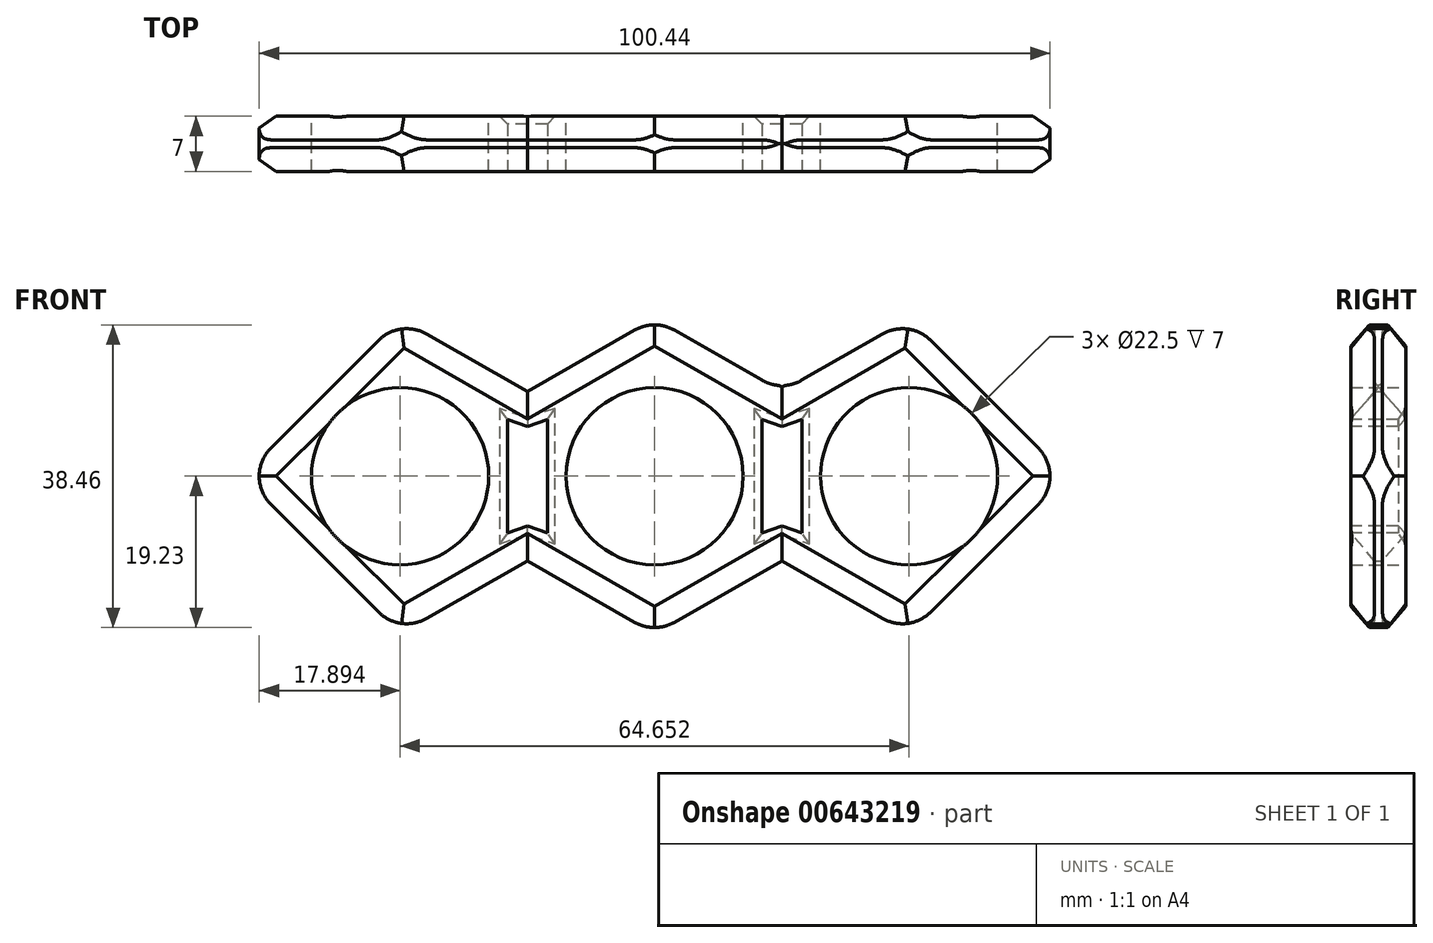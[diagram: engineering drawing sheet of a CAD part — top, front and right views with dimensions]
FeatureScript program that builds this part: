
annotation { "Feature Type Name" : "Feature", "Feature Type Description" : "" }
export const myFeature = defineFeature(function(context is Context, id is Id, definition is map)
    precondition{}
    {
        {
            var Q0;
            Q0=qCreatedBy(makeId("Front.planeOp"),FACE);
            var sketch = newSketch(context, id + "F0", { "sketchPlane" : qUnion([Q0])});
            skCircle(sketch, "E0", {"center": v(0, 0) * mm, "radius": 11.25 * mm});
            skCircle(sketch, "E1", {"center": v(-32.33, 0) * mm, "radius": 11.25 * mm});
            skCircle(sketch, "E2", {"center": v(32.33, 0) * mm, "radius": 11.25 * mm});
            skLineSegment(sketch, "E3", {"start": v(-32.33, 0) * mm, "end": v(-52.33, 0) * mm});
            skLineSegment(sketch, "E4.MirrorCS", {"start": v(32.33, 0) * mm, "end": v(52.33, 0) * mm});
            skLineSegment(sketch, "E5", {"start": v(-32.33, 0) * mm, "end": v(-32.33, 20) * mm});
            skLineSegment(sketch, "E6", {"start": v(-32.33, 0) * mm, "end": v(-32.33, -20) * mm});
            skLineSegment(sketch, "E7", {"start": v(-52.33, 0) * mm, "end": v(-32.33, -20) * mm});
            skLineSegment(sketch, "E8", {"start": v(-52.33, 0) * mm, "end": v(-32.33, 20) * mm});
            skLineSegment(sketch, "E9", {"start": v(-16.16, 0) * mm, "end": v(-16.16, 10.75) * mm});
            skLineSegment(sketch, "E10", {"start": v(-16.16, 10.75) * mm, "end": v(-32.33, 20) * mm});
            skLineSegment(sketch, "E11.MirrorCS", {"start": v(-16.16, -10.75) * mm, "end": v(-32.33, -20) * mm});
            skLineSegment(sketch, "E12.MirrorCS", {"start": v(-16.16, 0) * mm, "end": v(-16.16, -10.75) * mm});
            skLineSegment(sketch, "E13", {"start": v(0, 0) * mm, "end": v(0, 20) * mm});
            skLineSegment(sketch, "E14", {"start": v(0, 0) * mm, "end": v(0, -20) * mm});
            skLineSegment(sketch, "E15", {"start": v(-16.16, 10.75) * mm, "end": v(0, 20) * mm});
            skLineSegment(sketch, "E16", {"start": v(-16.16, -10.75) * mm, "end": v(0, -20) * mm});
            skLineSegment(sketch, "E17.MirrorCS", {"start": v(16.16, 10.75) * mm, "end": v(0, 20) * mm});
            skLineSegment(sketch, "E18.MirrorCS", {"start": v(16.16, -10.75) * mm, "end": v(0, -20) * mm});
            skLineSegment(sketch, "E19.MirrorCS", {"start": v(52.33, 0) * mm, "end": v(32.33, -20) * mm});
            skLineSegment(sketch, "E20.MirrorCS", {"start": v(52.33, 0) * mm, "end": v(32.33, 20) * mm});
            skLineSegment(sketch, "E21.MirrorCS", {"start": v(16.16, 10.75) * mm, "end": v(32.33, 20) * mm});
            skLineSegment(sketch, "E22.MirrorCS", {"start": v(16.16, -10.75) * mm, "end": v(32.33, -20) * mm});
            skLineSegment(sketch, "E23.MirrorCS", {"start": v(16.16, 0) * mm, "end": v(16.16, 10.75) * mm});
            skLineSegment(sketch, "E24.MirrorCS", {"start": v(16.16, 0) * mm, "end": v(16.16, -10.75) * mm});
            skLineSegment(sketch, "E25", {"start": v(-21.08, 0) * mm, "end": v(-11.25, 0) * mm});
            skLineSegment(sketch, "E26", {"start": v(11.25, 0) * mm, "end": v(21.08, 0) * mm});
            skSolve(sketch);
        }
        {
            var Q0;
            {var subQ0=sQuery(id+"F0.wireOp",EDGE,"E20.MirrorCS");Q0=makeQuery(id+"F0.imprint","IMPRINT",FACE,{"disambiguationData":[TD([[makeQuery(id+"F0.imprint","IMPRINT",EDGE,{"derivedFrom":subQ0}),1.0]])]});}
            var Q1;
            {var subQ0=sQuery(id+"F0.wireOp",EDGE,"E19.MirrorCS");Q1=makeQuery(id+"F0.imprint","IMPRINT",FACE,{"disambiguationData":[TD([[makeQuery(id+"F0.imprint","IMPRINT",EDGE,{"derivedFrom":subQ0}),-1.0]])]});}
            var Q2;
            {var subQ0=sQuery(id+"F0.wireOp",EDGE,"E18.MirrorCS");Q2=makeQuery(id+"F0.imprint","IMPRINT",FACE,{"disambiguationData":[TD([[makeQuery(id+"F0.imprint","IMPRINT",EDGE,{"derivedFrom":subQ0}),-1.0]])]});}
            var Q3;
            {var subQ0=sQuery(id+"F0.wireOp",EDGE,"E17.MirrorCS");Q3=makeQuery(id+"F0.imprint","IMPRINT",FACE,{"disambiguationData":[TD([[makeQuery(id+"F0.imprint","IMPRINT",EDGE,{"derivedFrom":subQ0}),1.0]])]});}
            var Q4;
            {var subQ4=sQuery(id+"F0.wireOp",EDGE,"E9");Q4=makeQuery(id+"F0.imprint","IMPRINT",FACE,{"disambiguationData":[TD([[makeQuery(id+"F0.imprint","IMPRINT",EDGE,{"derivedFrom":subQ4}),-1.0]])]});}
            var Q5;
            {var subQ0=sQuery(id+"F0.wireOp",EDGE,"E12.MirrorCS");Q5=makeQuery(id+"F0.imprint","IMPRINT",FACE,{"disambiguationData":[TD([[makeQuery(id+"F0.imprint","IMPRINT",EDGE,{"derivedFrom":subQ0}),1.0]])]});}
            var Q6;
            {var subQ0=sQuery(id+"F0.wireOp",EDGE,"E11.MirrorCS");Q6=makeQuery(id+"F0.imprint","IMPRINT",FACE,{"disambiguationData":[TD([[makeQuery(id+"F0.imprint","IMPRINT",EDGE,{"derivedFrom":subQ0}),-1.0]])]});}
            var Q7;
            {var subQ5=sQuery(id+"F0.wireOp",EDGE,"E7");Q7=makeQuery(id+"F0.imprint","IMPRINT",FACE,{"disambiguationData":[TD([[makeQuery(id+"F0.imprint","IMPRINT",EDGE,{"derivedFrom":subQ5}),1.0]])]});}
            var Q8;
            {var subQ5=sQuery(id+"F0.wireOp",EDGE,"E8");Q8=makeQuery(id+"F0.imprint","IMPRINT",FACE,{"disambiguationData":[TD([[makeQuery(id+"F0.imprint","IMPRINT",EDGE,{"derivedFrom":subQ5}),-1.0]])]});}
            var Q9;
            {var subQ0=sQuery(id+"F0.wireOp",EDGE,"E9");Q9=makeQuery(id+"F0.imprint","IMPRINT",FACE,{"disambiguationData":[TD([[makeQuery(id+"F0.imprint","IMPRINT",EDGE,{"derivedFrom":subQ0}),1.0]])]});}
            extrude(context, id + "F1", {"entities" : qUnion([Q0, Q1, Q2, Q3, Q4, Q5, Q6, Q7, Q8, Q9]), "depth" : 7 * mm, "offsetDistance" : 25.4 * mm});
        }
        {
            var Q0;
            Q0=makeQuery(id+"F1.opExtrude","CAP_FACE",FACE,{"disambiguationData":[OSD([sQuery(id+"F0.wireOp",EDGE,"E0"),sQuery(id+"F0.wireOp",EDGE,"E1"),sQuery(id+"F0.wireOp",EDGE,"E2"),sQuery(id+"F0.wireOp",EDGE,"E7"),sQuery(id+"F0.wireOp",EDGE,"E8"),sQuery(id+"F0.wireOp",EDGE,"E10"),sQuery(id+"F0.wireOp",EDGE,"E11.MirrorCS"),sQuery(id+"F0.wireOp",EDGE,"E15"),sQuery(id+"F0.wireOp",EDGE,"E16"),sQuery(id+"F0.wireOp",EDGE,"E17.MirrorCS"),sQuery(id+"F0.wireOp",EDGE,"E18.MirrorCS"),sQuery(id+"F0.wireOp",EDGE,"E19.MirrorCS"),sQuery(id+"F0.wireOp",EDGE,"E20.MirrorCS"),sQuery(id+"F0.wireOp",EDGE,"E21.MirrorCS"),sQuery(id+"F0.wireOp",EDGE,"E22.MirrorCS")])],"isStart":false});
            var sketch = newSketch(context, id + "F2", { "sketchPlane" : qUnion([Q0])});
            skLineSegment(sketch, "E27", {"start": v(16.16, -8.44) * mm, "end": v(16.16, 8.44) * mm});
            skLineSegment(sketch, "E28", {"start": v(-16.16, -8.44) * mm, "end": v(-16.16, 8.44) * mm});
            skLineSegment(sketch, "E29", {"start": v(13.63, -9.9) * mm, "end": v(13.63, 9.9) * mm});
            skLineSegment(sketch, "E30", {"start": v(13.63, 9.9) * mm, "end": v(18.7, 9.9) * mm});
            skLineSegment(sketch, "E31", {"start": v(18.7, 9.9) * mm, "end": v(18.7, -9.9) * mm});
            skLineSegment(sketch, "E32", {"start": v(13.63, -9.9) * mm, "end": v(16.16, -8.44) * mm});
            skLineSegment(sketch, "E33", {"start": v(16.16, -8.44) * mm, "end": v(18.7, -9.9) * mm});
            skLineSegment(sketch, "E34", {"start": v(13.63, 9.9) * mm, "end": v(16.16, 8.44) * mm});
            skLineSegment(sketch, "E35", {"start": v(16.16, 8.44) * mm, "end": v(18.7, 9.9) * mm});
            skLineSegment(sketch, "E36.MirrorCS", {"start": v(-13.63, -9.9) * mm, "end": v(-13.63, 9.9) * mm});
            skLineSegment(sketch, "E37.MirrorCS", {"start": v(-18.7, 9.9) * mm, "end": v(-18.7, -9.9) * mm});
            skLineSegment(sketch, "E38.MirrorCS", {"start": v(-16.16, 8.44) * mm, "end": v(-18.7, 9.9) * mm});
            skLineSegment(sketch, "E39.MirrorCS", {"start": v(-13.63, 9.9) * mm, "end": v(-16.16, 8.44) * mm});
            skLineSegment(sketch, "E40.MirrorCS", {"start": v(-16.16, -8.44) * mm, "end": v(-18.7, -9.9) * mm});
            skLineSegment(sketch, "E41.MirrorCS", {"start": v(-13.63, -9.9) * mm, "end": v(-16.16, -8.44) * mm});
            skLineSegment(sketch, "E42", {"start": v(-18.7, 7.21) * mm, "end": v(-16.16, 6.34) * mm});
            skLineSegment(sketch, "E43", {"start": v(-16.16, 6.34) * mm, "end": v(-13.63, 7.21) * mm});
            skLineSegment(sketch, "E44.MirrorCS", {"start": v(-16.16, -6.34) * mm, "end": v(-13.63, -7.21) * mm});
            skLineSegment(sketch, "E45.MirrorCS", {"start": v(-18.7, -7.21) * mm, "end": v(-16.16, -6.34) * mm});
            skLineSegment(sketch, "E46.MirrorCS", {"start": v(16.16, 6.34) * mm, "end": v(13.63, 7.21) * mm});
            skLineSegment(sketch, "E47.MirrorCS", {"start": v(18.7, 7.21) * mm, "end": v(16.16, 6.34) * mm});
            skLineSegment(sketch, "E48.MirrorCS", {"start": v(16.16, -6.34) * mm, "end": v(13.63, -7.21) * mm});
            skLineSegment(sketch, "E49.MirrorCS", {"start": v(18.7, -7.21) * mm, "end": v(16.16, -6.34) * mm});
            skSolve(sketch);
        }
        {
            var Q0;
            {var subQ0=sQuery(id+"F2.wireOp",EDGE,"E43");Q0=makeQuery(id+"F2.imprint","IMPRINT",FACE,{"disambiguationData":[TD([[makeQuery(id+"F2.imprint","IMPRINT",EDGE,{"derivedFrom":subQ0}),-1.0]])]});}
            var Q1;
            {var subQ0=sQuery(id+"F2.wireOp",EDGE,"E42");Q1=makeQuery(id+"F2.imprint","IMPRINT",FACE,{"disambiguationData":[TD([[makeQuery(id+"F2.imprint","IMPRINT",EDGE,{"derivedFrom":subQ0}),-1.0]])]});}
            var Q2;
            {var subQ0=sQuery(id+"F2.wireOp",EDGE,"E46.MirrorCS");Q2=makeQuery(id+"F2.imprint","IMPRINT",FACE,{"disambiguationData":[TD([[makeQuery(id+"F2.imprint","IMPRINT",EDGE,{"derivedFrom":subQ0}),1.0]])]});}
            var Q3;
            {var subQ0=sQuery(id+"F2.wireOp",EDGE,"E47.MirrorCS");Q3=makeQuery(id+"F2.imprint","IMPRINT",FACE,{"disambiguationData":[TD([[makeQuery(id+"F2.imprint","IMPRINT",EDGE,{"derivedFrom":subQ0}),1.0]])]});}
            extrude(context, id + "F3", {"entities" : qUnion([Q0, Q1, Q2, Q3]), "operationType" : NewBodyOperationType.REMOVE, "oppositeDirection" : true, "depth" : 127 * mm, "offsetDistance" : 25.4 * mm});
        }
        {
            var Q0;
            Q0=makeQuery(id+"F1.opExtrude","CAP_EDGE",EDGE,{"disambiguationData":[OSD([sQuery(id+"F0.wireOp",EDGE,"E10")])],"isStart":false});
            var Q1;
            Q1=makeQuery(id+"F1.opExtrude","CAP_EDGE",EDGE,{"disambiguationData":[OSD([sQuery(id+"F0.wireOp",EDGE,"E15")])],"isStart":false});
            var Q2;
            Q2=makeQuery(id+"F1.opExtrude","CAP_EDGE",EDGE,{"disambiguationData":[OSD([sQuery(id+"F0.wireOp",EDGE,"E17.MirrorCS")])],"isStart":false});
            var Q3;
            Q3=makeQuery(id+"F1.opExtrude","CAP_EDGE",EDGE,{"disambiguationData":[OSD([sQuery(id+"F0.wireOp",EDGE,"E21.MirrorCS")])],"isStart":false});
            var Q4;
            Q4=makeQuery(id+"F1.opExtrude","CAP_EDGE",EDGE,{"disambiguationData":[OSD([sQuery(id+"F0.wireOp",EDGE,"E20.MirrorCS")])],"isStart":false});
            var Q5;
            Q5=makeQuery(id+"F1.opExtrude","CAP_EDGE",EDGE,{"disambiguationData":[OSD([sQuery(id+"F0.wireOp",EDGE,"E20.MirrorCS")])],"isStart":true});
            var Q6;
            Q6=makeQuery(id+"F1.opExtrude","CAP_EDGE",EDGE,{"disambiguationData":[OSD([sQuery(id+"F0.wireOp",EDGE,"E21.MirrorCS")])],"isStart":true});
            var Q7;
            Q7=makeQuery(id+"F1.opExtrude","CAP_EDGE",EDGE,{"disambiguationData":[OSD([sQuery(id+"F0.wireOp",EDGE,"E17.MirrorCS")])],"isStart":true});
            var Q8;
            Q8=makeQuery(id+"F1.opExtrude","CAP_EDGE",EDGE,{"disambiguationData":[OSD([sQuery(id+"F0.wireOp",EDGE,"E15")])],"isStart":true});
            var Q9;
            Q9=makeQuery(id+"F1.opExtrude","CAP_EDGE",EDGE,{"disambiguationData":[OSD([sQuery(id+"F0.wireOp",EDGE,"E10")])],"isStart":true});
            var Q10;
            Q10=makeQuery(id+"F1.opExtrude","CAP_EDGE",EDGE,{"disambiguationData":[OSD([sQuery(id+"F0.wireOp",EDGE,"E8")])],"isStart":false});
            var Q11;
            Q11=makeQuery(id+"F1.opExtrude","CAP_EDGE",EDGE,{"disambiguationData":[OSD([sQuery(id+"F0.wireOp",EDGE,"E8")])],"isStart":true});
            var Q12;
            Q12=makeQuery(id+"F1.opExtrude","CAP_EDGE",EDGE,{"disambiguationData":[OSD([sQuery(id+"F0.wireOp",EDGE,"E7")])],"isStart":false});
            var Q13;
            Q13=makeQuery(id+"F1.opExtrude","CAP_EDGE",EDGE,{"disambiguationData":[OSD([sQuery(id+"F0.wireOp",EDGE,"E7")])],"isStart":true});
            var Q14;
            Q14=makeQuery(id+"F1.opExtrude","CAP_EDGE",EDGE,{"disambiguationData":[OSD([sQuery(id+"F0.wireOp",EDGE,"E11.MirrorCS")])],"isStart":true});
            var Q15;
            Q15=makeQuery(id+"F1.opExtrude","CAP_EDGE",EDGE,{"disambiguationData":[OSD([sQuery(id+"F0.wireOp",EDGE,"E11.MirrorCS")])],"isStart":false});
            var Q16;
            Q16=makeQuery(id+"F1.opExtrude","CAP_EDGE",EDGE,{"disambiguationData":[OSD([sQuery(id+"F0.wireOp",EDGE,"E16")])],"isStart":false});
            var Q17;
            Q17=makeQuery(id+"F1.opExtrude","CAP_EDGE",EDGE,{"disambiguationData":[OSD([sQuery(id+"F0.wireOp",EDGE,"E16")])],"isStart":true});
            var Q18;
            Q18=makeQuery(id+"F1.opExtrude","CAP_EDGE",EDGE,{"disambiguationData":[OSD([sQuery(id+"F0.wireOp",EDGE,"E18.MirrorCS")])],"isStart":true});
            var Q19;
            Q19=makeQuery(id+"F1.opExtrude","CAP_EDGE",EDGE,{"disambiguationData":[OSD([sQuery(id+"F0.wireOp",EDGE,"E18.MirrorCS")])],"isStart":false});
            var Q20;
            Q20=makeQuery(id+"F1.opExtrude","CAP_EDGE",EDGE,{"disambiguationData":[OSD([sQuery(id+"F0.wireOp",EDGE,"E22.MirrorCS")])],"isStart":true});
            var Q21;
            Q21=makeQuery(id+"F1.opExtrude","CAP_EDGE",EDGE,{"disambiguationData":[OSD([sQuery(id+"F0.wireOp",EDGE,"E22.MirrorCS")])],"isStart":false});
            var Q22;
            Q22=makeQuery(id+"F1.opExtrude","CAP_EDGE",EDGE,{"disambiguationData":[OSD([sQuery(id+"F0.wireOp",EDGE,"E19.MirrorCS")])],"isStart":true});
            var Q23;
            Q23=makeQuery(id+"F1.opExtrude","CAP_EDGE",EDGE,{"disambiguationData":[OSD([sQuery(id+"F0.wireOp",EDGE,"E19.MirrorCS")])],"isStart":false});
            chamfer(context, id + "F4", {"entities" : qUnion([Q0, Q1, Q2, Q3, Q4, Q5, Q6, Q7, Q8, Q9, Q10, Q11, Q12, Q13, Q14, Q15, Q16, Q17, Q18, Q19, Q20, Q21, Q22, Q23]), "width" : 3 * mm, "tangentPropagation" : true});
        }
        {
            var Q0;
            Q0=makeQuery(id+"F1.opExtrude","SWEPT_EDGE",EDGE,{"disambiguationData":[OSD([sQuery(id+"F0.wireOp",EDGE,"E3"),sQuery(id+"F0.wireOp",EDGE,"E7"),sQuery(id+"F0.wireOp",EDGE,"E8")])]});
            var Q1;
            Q1=makeQuery(id+"F1.opExtrude","SWEPT_EDGE",EDGE,{"disambiguationData":[OSD([sQuery(id+"F0.wireOp",EDGE,"E6"),sQuery(id+"F0.wireOp",EDGE,"E7"),sQuery(id+"F0.wireOp",EDGE,"E11.MirrorCS")])]});
            var Q2;
            Q2=makeQuery(id+"F1.opExtrude","SWEPT_EDGE",EDGE,{"disambiguationData":[OSD([sQuery(id+"F0.wireOp",EDGE,"E14"),sQuery(id+"F0.wireOp",EDGE,"E16"),sQuery(id+"F0.wireOp",EDGE,"E18.MirrorCS")])]});
            var Q3;
            Q3=makeQuery(id+"F1.opExtrude","SWEPT_EDGE",EDGE,{"disambiguationData":[OSD([sQuery(id+"F0.wireOp",EDGE,"E19.MirrorCS"),sQuery(id+"F0.wireOp",EDGE,"E22.MirrorCS")])]});
            var Q4;
            Q4=makeQuery(id+"F1.opExtrude","SWEPT_EDGE",EDGE,{"disambiguationData":[OSD([sQuery(id+"F0.wireOp",EDGE,"E4.MirrorCS"),sQuery(id+"F0.wireOp",EDGE,"E19.MirrorCS"),sQuery(id+"F0.wireOp",EDGE,"E20.MirrorCS")])]});
            var Q5;
            Q5=makeQuery(id+"F1.opExtrude","SWEPT_EDGE",EDGE,{"disambiguationData":[OSD([sQuery(id+"F0.wireOp",EDGE,"E20.MirrorCS"),sQuery(id+"F0.wireOp",EDGE,"E21.MirrorCS")])]});
            var Q6;
            Q6=makeQuery(id+"F1.opExtrude","SWEPT_EDGE",EDGE,{"disambiguationData":[OSD([sQuery(id+"F0.wireOp",EDGE,"E17.MirrorCS"),sQuery(id+"F0.wireOp",EDGE,"E21.MirrorCS"),sQuery(id+"F0.wireOp",EDGE,"E23.MirrorCS")])]});
            var Q7;
            Q7=makeQuery(id+"F1.opExtrude","SWEPT_EDGE",EDGE,{"disambiguationData":[OSD([sQuery(id+"F0.wireOp",EDGE,"E13"),sQuery(id+"F0.wireOp",EDGE,"E15"),sQuery(id+"F0.wireOp",EDGE,"E17.MirrorCS")])]});
            var Q8;
            Q8=makeQuery(id+"F1.opExtrude","SWEPT_EDGE",EDGE,{"disambiguationData":[OSD([sQuery(id+"F0.wireOp",EDGE,"E5"),sQuery(id+"F0.wireOp",EDGE,"E8"),sQuery(id+"F0.wireOp",EDGE,"E10")])]});
            fillet(context, id + "F5", {"entities" : qUnion([Q0, Q1, Q2, Q3, Q4, Q5, Q6, Q7, Q8]), "radius" : 5.08 * mm, "tangentPropagation" : true, "allowEdgeOverflow" : false});
        }
        {
            var Q0;
            Q0=makeQuery(id+"F3.boolean.opBoolean","INTERSECT",EDGE,{"derivedFrom":[makeQuery(id+"F1.opExtrude","CAP_FACE",FACE,{"disambiguationData":[OSD([sQuery(id+"F0.wireOp",EDGE,"E0"),sQuery(id+"F0.wireOp",EDGE,"E1"),sQuery(id+"F0.wireOp",EDGE,"E2"),sQuery(id+"F0.wireOp",EDGE,"E7"),sQuery(id+"F0.wireOp",EDGE,"E8"),sQuery(id+"F0.wireOp",EDGE,"E10"),sQuery(id+"F0.wireOp",EDGE,"E11.MirrorCS"),sQuery(id+"F0.wireOp",EDGE,"E15"),sQuery(id+"F0.wireOp",EDGE,"E16"),sQuery(id+"F0.wireOp",EDGE,"E17.MirrorCS"),sQuery(id+"F0.wireOp",EDGE,"E18.MirrorCS"),sQuery(id+"F0.wireOp",EDGE,"E19.MirrorCS"),sQuery(id+"F0.wireOp",EDGE,"E20.MirrorCS"),sQuery(id+"F0.wireOp",EDGE,"E21.MirrorCS"),sQuery(id+"F0.wireOp",EDGE,"E22.MirrorCS")])],"isStart":true}),makeQuery(id+"F3.opExtrude","SWEPT_FACE",FACE,{"disambiguationData":[OSD([sQuery(id+"F2.wireOp",EDGE,"E36.MirrorCS")])]})]});
            var Q1;
            Q1=makeQuery(id+"F3.boolean.opBoolean","INTERSECT",EDGE,{"derivedFrom":[makeQuery(id+"F1.opExtrude","CAP_FACE",FACE,{"disambiguationData":[OSD([sQuery(id+"F0.wireOp",EDGE,"E0"),sQuery(id+"F0.wireOp",EDGE,"E1"),sQuery(id+"F0.wireOp",EDGE,"E2"),sQuery(id+"F0.wireOp",EDGE,"E7"),sQuery(id+"F0.wireOp",EDGE,"E8"),sQuery(id+"F0.wireOp",EDGE,"E10"),sQuery(id+"F0.wireOp",EDGE,"E11.MirrorCS"),sQuery(id+"F0.wireOp",EDGE,"E15"),sQuery(id+"F0.wireOp",EDGE,"E16"),sQuery(id+"F0.wireOp",EDGE,"E17.MirrorCS"),sQuery(id+"F0.wireOp",EDGE,"E18.MirrorCS"),sQuery(id+"F0.wireOp",EDGE,"E19.MirrorCS"),sQuery(id+"F0.wireOp",EDGE,"E20.MirrorCS"),sQuery(id+"F0.wireOp",EDGE,"E21.MirrorCS"),sQuery(id+"F0.wireOp",EDGE,"E22.MirrorCS")])],"isStart":true}),makeQuery(id+"F3.opExtrude","SWEPT_FACE",FACE,{"disambiguationData":[OSD([sQuery(id+"F2.wireOp",EDGE,"E37.MirrorCS")])]})]});
            var Q2;
            Q2=makeQuery(id+"F3.boolean.opBoolean","COPY",EDGE,{"derivedFrom":makeQuery(id+"F3.opExtrude","CAP_EDGE",EDGE,{"disambiguationData":[OSD([sQuery(id+"F2.wireOp",EDGE,"E37.MirrorCS")])],"isStart":true})});
            var Q3;
            Q3=makeQuery(id+"F3.boolean.opBoolean","COPY",EDGE,{"derivedFrom":makeQuery(id+"F3.opExtrude","CAP_EDGE",EDGE,{"disambiguationData":[OSD([sQuery(id+"F2.wireOp",EDGE,"E36.MirrorCS")])],"isStart":true})});
            var Q4;
            Q4=makeQuery(id+"F3.boolean.opBoolean","COPY",EDGE,{"derivedFrom":makeQuery(id+"F3.opExtrude","CAP_EDGE",EDGE,{"disambiguationData":[OSD([sQuery(id+"F2.wireOp",EDGE,"E29")])],"isStart":true})});
            var Q5;
            Q5=makeQuery(id+"F3.boolean.opBoolean","COPY",EDGE,{"derivedFrom":makeQuery(id+"F3.opExtrude","CAP_EDGE",EDGE,{"disambiguationData":[OSD([sQuery(id+"F2.wireOp",EDGE,"E31")])],"isStart":true})});
            var Q6;
            Q6=makeQuery(id+"F3.boolean.opBoolean","INTERSECT",EDGE,{"derivedFrom":[makeQuery(id+"F1.opExtrude","CAP_FACE",FACE,{"disambiguationData":[OSD([sQuery(id+"F0.wireOp",EDGE,"E0"),sQuery(id+"F0.wireOp",EDGE,"E1"),sQuery(id+"F0.wireOp",EDGE,"E2"),sQuery(id+"F0.wireOp",EDGE,"E7"),sQuery(id+"F0.wireOp",EDGE,"E8"),sQuery(id+"F0.wireOp",EDGE,"E10"),sQuery(id+"F0.wireOp",EDGE,"E11.MirrorCS"),sQuery(id+"F0.wireOp",EDGE,"E15"),sQuery(id+"F0.wireOp",EDGE,"E16"),sQuery(id+"F0.wireOp",EDGE,"E17.MirrorCS"),sQuery(id+"F0.wireOp",EDGE,"E18.MirrorCS"),sQuery(id+"F0.wireOp",EDGE,"E19.MirrorCS"),sQuery(id+"F0.wireOp",EDGE,"E20.MirrorCS"),sQuery(id+"F0.wireOp",EDGE,"E21.MirrorCS"),sQuery(id+"F0.wireOp",EDGE,"E22.MirrorCS")])],"isStart":true}),makeQuery(id+"F3.opExtrude","SWEPT_FACE",FACE,{"disambiguationData":[OSD([sQuery(id+"F2.wireOp",EDGE,"E31")])]})]});
            var Q7;
            Q7=makeQuery(id+"F3.boolean.opBoolean","INTERSECT",EDGE,{"derivedFrom":[makeQuery(id+"F1.opExtrude","CAP_FACE",FACE,{"disambiguationData":[OSD([sQuery(id+"F0.wireOp",EDGE,"E0"),sQuery(id+"F0.wireOp",EDGE,"E1"),sQuery(id+"F0.wireOp",EDGE,"E2"),sQuery(id+"F0.wireOp",EDGE,"E7"),sQuery(id+"F0.wireOp",EDGE,"E8"),sQuery(id+"F0.wireOp",EDGE,"E10"),sQuery(id+"F0.wireOp",EDGE,"E11.MirrorCS"),sQuery(id+"F0.wireOp",EDGE,"E15"),sQuery(id+"F0.wireOp",EDGE,"E16"),sQuery(id+"F0.wireOp",EDGE,"E17.MirrorCS"),sQuery(id+"F0.wireOp",EDGE,"E18.MirrorCS"),sQuery(id+"F0.wireOp",EDGE,"E19.MirrorCS"),sQuery(id+"F0.wireOp",EDGE,"E20.MirrorCS"),sQuery(id+"F0.wireOp",EDGE,"E21.MirrorCS"),sQuery(id+"F0.wireOp",EDGE,"E22.MirrorCS")])],"isStart":true}),makeQuery(id+"F3.opExtrude","SWEPT_FACE",FACE,{"disambiguationData":[OSD([sQuery(id+"F2.wireOp",EDGE,"E29")])]})]});
            var Q8;
            {var subQ0=sQuery(id+"F0.wireOp",EDGE,"E21.MirrorCS");Q8=makeQuery(id+"F5.opFillet","BLEND_EDGE",EDGE,{"blendedFrom":[makeQuery(id+"F1.opExtrude","SWEPT_EDGE",EDGE,{"disambiguationData":[OSD([sQuery(id+"F0.wireOp",EDGE,"E17.MirrorCS"),subQ0,sQuery(id+"F0.wireOp",EDGE,"E23.MirrorCS")])]}),makeQuery(id+"F1.opExtrude","SWEPT_FACE",FACE,{"disambiguationData":[OSD([subQ0])]})],"blendedInto":[makeQuery(id+"F1.opExtrude","SWEPT_FACE",FACE,{"disambiguationData":[OSD([subQ0])]})]});}
            var Q9;
            Q9=makeQuery(id+"F3.boolean.opBoolean","INTERSECT",EDGE,{"derivedFrom":[makeQuery(id+"F1.opExtrude","CAP_FACE",FACE,{"disambiguationData":[OSD([sQuery(id+"F0.wireOp",EDGE,"E0"),sQuery(id+"F0.wireOp",EDGE,"E1"),sQuery(id+"F0.wireOp",EDGE,"E2"),sQuery(id+"F0.wireOp",EDGE,"E7"),sQuery(id+"F0.wireOp",EDGE,"E8"),sQuery(id+"F0.wireOp",EDGE,"E10"),sQuery(id+"F0.wireOp",EDGE,"E11.MirrorCS"),sQuery(id+"F0.wireOp",EDGE,"E15"),sQuery(id+"F0.wireOp",EDGE,"E16"),sQuery(id+"F0.wireOp",EDGE,"E17.MirrorCS"),sQuery(id+"F0.wireOp",EDGE,"E18.MirrorCS"),sQuery(id+"F0.wireOp",EDGE,"E19.MirrorCS"),sQuery(id+"F0.wireOp",EDGE,"E20.MirrorCS"),sQuery(id+"F0.wireOp",EDGE,"E21.MirrorCS"),sQuery(id+"F0.wireOp",EDGE,"E22.MirrorCS")])],"isStart":true}),makeQuery(id+"F3.opExtrude","SWEPT_FACE",FACE,{"disambiguationData":[OSD([sQuery(id+"F2.wireOp",EDGE,"E49.MirrorCS")])]})]});
            var Q10;
            Q10=makeQuery(id+"F3.boolean.opBoolean","INTERSECT",EDGE,{"derivedFrom":[makeQuery(id+"F1.opExtrude","CAP_FACE",FACE,{"disambiguationData":[OSD([sQuery(id+"F0.wireOp",EDGE,"E0"),sQuery(id+"F0.wireOp",EDGE,"E1"),sQuery(id+"F0.wireOp",EDGE,"E2"),sQuery(id+"F0.wireOp",EDGE,"E7"),sQuery(id+"F0.wireOp",EDGE,"E8"),sQuery(id+"F0.wireOp",EDGE,"E10"),sQuery(id+"F0.wireOp",EDGE,"E11.MirrorCS"),sQuery(id+"F0.wireOp",EDGE,"E15"),sQuery(id+"F0.wireOp",EDGE,"E16"),sQuery(id+"F0.wireOp",EDGE,"E17.MirrorCS"),sQuery(id+"F0.wireOp",EDGE,"E18.MirrorCS"),sQuery(id+"F0.wireOp",EDGE,"E19.MirrorCS"),sQuery(id+"F0.wireOp",EDGE,"E20.MirrorCS"),sQuery(id+"F0.wireOp",EDGE,"E21.MirrorCS"),sQuery(id+"F0.wireOp",EDGE,"E22.MirrorCS")])],"isStart":true}),makeQuery(id+"F3.opExtrude","SWEPT_FACE",FACE,{"disambiguationData":[OSD([sQuery(id+"F2.wireOp",EDGE,"E48.MirrorCS")])]})]});
            var Q11;
            Q11=makeQuery(id+"F3.boolean.opBoolean","INTERSECT",EDGE,{"derivedFrom":[makeQuery(id+"F1.opExtrude","CAP_FACE",FACE,{"disambiguationData":[OSD([sQuery(id+"F0.wireOp",EDGE,"E0"),sQuery(id+"F0.wireOp",EDGE,"E1"),sQuery(id+"F0.wireOp",EDGE,"E2"),sQuery(id+"F0.wireOp",EDGE,"E7"),sQuery(id+"F0.wireOp",EDGE,"E8"),sQuery(id+"F0.wireOp",EDGE,"E10"),sQuery(id+"F0.wireOp",EDGE,"E11.MirrorCS"),sQuery(id+"F0.wireOp",EDGE,"E15"),sQuery(id+"F0.wireOp",EDGE,"E16"),sQuery(id+"F0.wireOp",EDGE,"E17.MirrorCS"),sQuery(id+"F0.wireOp",EDGE,"E18.MirrorCS"),sQuery(id+"F0.wireOp",EDGE,"E19.MirrorCS"),sQuery(id+"F0.wireOp",EDGE,"E20.MirrorCS"),sQuery(id+"F0.wireOp",EDGE,"E21.MirrorCS"),sQuery(id+"F0.wireOp",EDGE,"E22.MirrorCS")])],"isStart":true}),makeQuery(id+"F3.opExtrude","SWEPT_FACE",FACE,{"disambiguationData":[OSD([sQuery(id+"F2.wireOp",EDGE,"E47.MirrorCS")])]})]});
            var Q12;
            Q12=makeQuery(id+"F3.boolean.opBoolean","INTERSECT",EDGE,{"derivedFrom":[makeQuery(id+"F1.opExtrude","CAP_FACE",FACE,{"disambiguationData":[OSD([sQuery(id+"F0.wireOp",EDGE,"E0"),sQuery(id+"F0.wireOp",EDGE,"E1"),sQuery(id+"F0.wireOp",EDGE,"E2"),sQuery(id+"F0.wireOp",EDGE,"E7"),sQuery(id+"F0.wireOp",EDGE,"E8"),sQuery(id+"F0.wireOp",EDGE,"E10"),sQuery(id+"F0.wireOp",EDGE,"E11.MirrorCS"),sQuery(id+"F0.wireOp",EDGE,"E15"),sQuery(id+"F0.wireOp",EDGE,"E16"),sQuery(id+"F0.wireOp",EDGE,"E17.MirrorCS"),sQuery(id+"F0.wireOp",EDGE,"E18.MirrorCS"),sQuery(id+"F0.wireOp",EDGE,"E19.MirrorCS"),sQuery(id+"F0.wireOp",EDGE,"E20.MirrorCS"),sQuery(id+"F0.wireOp",EDGE,"E21.MirrorCS"),sQuery(id+"F0.wireOp",EDGE,"E22.MirrorCS")])],"isStart":true}),makeQuery(id+"F3.opExtrude","SWEPT_FACE",FACE,{"disambiguationData":[OSD([sQuery(id+"F2.wireOp",EDGE,"E46.MirrorCS")])]})]});
            var Q13;
            Q13=makeQuery(id+"F3.boolean.opBoolean","COPY",EDGE,{"derivedFrom":makeQuery(id+"F3.opExtrude","CAP_EDGE",EDGE,{"disambiguationData":[OSD([sQuery(id+"F2.wireOp",EDGE,"E46.MirrorCS")])],"isStart":true})});
            var Q14;
            Q14=makeQuery(id+"F3.boolean.opBoolean","COPY",EDGE,{"derivedFrom":makeQuery(id+"F3.opExtrude","CAP_EDGE",EDGE,{"disambiguationData":[OSD([sQuery(id+"F2.wireOp",EDGE,"E47.MirrorCS")])],"isStart":true})});
            var Q15;
            Q15=makeQuery(id+"F3.boolean.opBoolean","COPY",EDGE,{"derivedFrom":makeQuery(id+"F3.opExtrude","CAP_EDGE",EDGE,{"disambiguationData":[OSD([sQuery(id+"F2.wireOp",EDGE,"E48.MirrorCS")])],"isStart":true})});
            var Q16;
            Q16=makeQuery(id+"F3.boolean.opBoolean","COPY",EDGE,{"derivedFrom":makeQuery(id+"F3.opExtrude","CAP_EDGE",EDGE,{"disambiguationData":[OSD([sQuery(id+"F2.wireOp",EDGE,"E49.MirrorCS")])],"isStart":true})});
            var Q17;
            Q17=makeQuery(id+"F3.boolean.opBoolean","COPY",EDGE,{"derivedFrom":makeQuery(id+"F3.opExtrude","CAP_EDGE",EDGE,{"disambiguationData":[OSD([sQuery(id+"F2.wireOp",EDGE,"E45.MirrorCS")])],"isStart":true})});
            var Q18;
            Q18=makeQuery(id+"F3.boolean.opBoolean","COPY",EDGE,{"derivedFrom":makeQuery(id+"F3.opExtrude","CAP_EDGE",EDGE,{"disambiguationData":[OSD([sQuery(id+"F2.wireOp",EDGE,"E44.MirrorCS")])],"isStart":true})});
            var Q19;
            Q19=makeQuery(id+"F3.boolean.opBoolean","COPY",EDGE,{"derivedFrom":makeQuery(id+"F3.opExtrude","CAP_EDGE",EDGE,{"disambiguationData":[OSD([sQuery(id+"F2.wireOp",EDGE,"E43")])],"isStart":true})});
            var Q20;
            Q20=makeQuery(id+"F3.boolean.opBoolean","COPY",EDGE,{"derivedFrom":makeQuery(id+"F3.opExtrude","CAP_EDGE",EDGE,{"disambiguationData":[OSD([sQuery(id+"F2.wireOp",EDGE,"E42")])],"isStart":true})});
            var Q21;
            Q21=makeQuery(id+"F3.boolean.opBoolean","INTERSECT",EDGE,{"derivedFrom":[makeQuery(id+"F1.opExtrude","CAP_FACE",FACE,{"disambiguationData":[OSD([sQuery(id+"F0.wireOp",EDGE,"E0"),sQuery(id+"F0.wireOp",EDGE,"E1"),sQuery(id+"F0.wireOp",EDGE,"E2"),sQuery(id+"F0.wireOp",EDGE,"E7"),sQuery(id+"F0.wireOp",EDGE,"E8"),sQuery(id+"F0.wireOp",EDGE,"E10"),sQuery(id+"F0.wireOp",EDGE,"E11.MirrorCS"),sQuery(id+"F0.wireOp",EDGE,"E15"),sQuery(id+"F0.wireOp",EDGE,"E16"),sQuery(id+"F0.wireOp",EDGE,"E17.MirrorCS"),sQuery(id+"F0.wireOp",EDGE,"E18.MirrorCS"),sQuery(id+"F0.wireOp",EDGE,"E19.MirrorCS"),sQuery(id+"F0.wireOp",EDGE,"E20.MirrorCS"),sQuery(id+"F0.wireOp",EDGE,"E21.MirrorCS"),sQuery(id+"F0.wireOp",EDGE,"E22.MirrorCS")])],"isStart":true}),makeQuery(id+"F3.opExtrude","SWEPT_FACE",FACE,{"disambiguationData":[OSD([sQuery(id+"F2.wireOp",EDGE,"E44.MirrorCS")])]})]});
            var Q22;
            Q22=makeQuery(id+"F3.boolean.opBoolean","INTERSECT",EDGE,{"derivedFrom":[makeQuery(id+"F1.opExtrude","CAP_FACE",FACE,{"disambiguationData":[OSD([sQuery(id+"F0.wireOp",EDGE,"E0"),sQuery(id+"F0.wireOp",EDGE,"E1"),sQuery(id+"F0.wireOp",EDGE,"E2"),sQuery(id+"F0.wireOp",EDGE,"E7"),sQuery(id+"F0.wireOp",EDGE,"E8"),sQuery(id+"F0.wireOp",EDGE,"E10"),sQuery(id+"F0.wireOp",EDGE,"E11.MirrorCS"),sQuery(id+"F0.wireOp",EDGE,"E15"),sQuery(id+"F0.wireOp",EDGE,"E16"),sQuery(id+"F0.wireOp",EDGE,"E17.MirrorCS"),sQuery(id+"F0.wireOp",EDGE,"E18.MirrorCS"),sQuery(id+"F0.wireOp",EDGE,"E19.MirrorCS"),sQuery(id+"F0.wireOp",EDGE,"E20.MirrorCS"),sQuery(id+"F0.wireOp",EDGE,"E21.MirrorCS"),sQuery(id+"F0.wireOp",EDGE,"E22.MirrorCS")])],"isStart":true}),makeQuery(id+"F3.opExtrude","SWEPT_FACE",FACE,{"disambiguationData":[OSD([sQuery(id+"F2.wireOp",EDGE,"E45.MirrorCS")])]})]});
            var Q23;
            Q23=makeQuery(id+"F3.boolean.opBoolean","INTERSECT",EDGE,{"derivedFrom":[makeQuery(id+"F1.opExtrude","CAP_FACE",FACE,{"disambiguationData":[OSD([sQuery(id+"F0.wireOp",EDGE,"E0"),sQuery(id+"F0.wireOp",EDGE,"E1"),sQuery(id+"F0.wireOp",EDGE,"E2"),sQuery(id+"F0.wireOp",EDGE,"E7"),sQuery(id+"F0.wireOp",EDGE,"E8"),sQuery(id+"F0.wireOp",EDGE,"E10"),sQuery(id+"F0.wireOp",EDGE,"E11.MirrorCS"),sQuery(id+"F0.wireOp",EDGE,"E15"),sQuery(id+"F0.wireOp",EDGE,"E16"),sQuery(id+"F0.wireOp",EDGE,"E17.MirrorCS"),sQuery(id+"F0.wireOp",EDGE,"E18.MirrorCS"),sQuery(id+"F0.wireOp",EDGE,"E19.MirrorCS"),sQuery(id+"F0.wireOp",EDGE,"E20.MirrorCS"),sQuery(id+"F0.wireOp",EDGE,"E21.MirrorCS"),sQuery(id+"F0.wireOp",EDGE,"E22.MirrorCS")])],"isStart":true}),makeQuery(id+"F3.opExtrude","SWEPT_FACE",FACE,{"disambiguationData":[OSD([sQuery(id+"F2.wireOp",EDGE,"E42")])]})]});
            var Q24;
            Q24=makeQuery(id+"F3.boolean.opBoolean","INTERSECT",EDGE,{"derivedFrom":[makeQuery(id+"F1.opExtrude","CAP_FACE",FACE,{"disambiguationData":[OSD([sQuery(id+"F0.wireOp",EDGE,"E0"),sQuery(id+"F0.wireOp",EDGE,"E1"),sQuery(id+"F0.wireOp",EDGE,"E2"),sQuery(id+"F0.wireOp",EDGE,"E7"),sQuery(id+"F0.wireOp",EDGE,"E8"),sQuery(id+"F0.wireOp",EDGE,"E10"),sQuery(id+"F0.wireOp",EDGE,"E11.MirrorCS"),sQuery(id+"F0.wireOp",EDGE,"E15"),sQuery(id+"F0.wireOp",EDGE,"E16"),sQuery(id+"F0.wireOp",EDGE,"E17.MirrorCS"),sQuery(id+"F0.wireOp",EDGE,"E18.MirrorCS"),sQuery(id+"F0.wireOp",EDGE,"E19.MirrorCS"),sQuery(id+"F0.wireOp",EDGE,"E20.MirrorCS"),sQuery(id+"F0.wireOp",EDGE,"E21.MirrorCS"),sQuery(id+"F0.wireOp",EDGE,"E22.MirrorCS")])],"isStart":true}),makeQuery(id+"F3.opExtrude","SWEPT_FACE",FACE,{"disambiguationData":[OSD([sQuery(id+"F2.wireOp",EDGE,"E43")])]})]});
            chamfer(context, id + "F6", {"entities" : qUnion([Q0, Q1, Q2, Q3, Q4, Q5, Q6, Q7, Q8, Q9, Q10, Q11, Q12, Q13, Q14, Q15, Q16, Q17, Q18, Q19, Q20, Q21, Q22, Q23, Q24]), "width" : 1 * mm, "tangentPropagation" : true});
        }
    });
